# Revit family: Chaine de traitement par Absorption (support au sol) - AD5325
name_source: partatom
category: Equipement spécialisé
revit_build: Autodesk Revit 2018 (Build: 20170223_1515(x64)
units: mm (PartAtom-declared; Revit-internal decimal feet)

## family parameters
Basée sur le plan de construction = Non
Cote de connecteur circulaire = Utiliser le diamètre
Couper avec des vides une fois chargée = Non
Partagée = Non
Point de calcul de pièce = Non
Toujours verticalement = Oui
Type d'élément = Normal

## types (1)
- SEC 7 HC - AD 5325
    COS_PHI = 0.9
    DEBIT_ENTREE_AIR = 325.0 m³/h
    DEBIT_SORTIE_AIR = 325.0 m³/h
    DESCR_ALIM_X = Alimentation X ; ID 3G1mm² ;
    DESCR_ENTREE_AIR = Entrée Air ; 325 m3/h à 10 bar ; ID G 1"1/4 ;
    DESCR_SORTIE_AIR = Sortie Air ; 325 m3/h à 10 bar ; ID G 1"1/4 ;
    DIAM_ENTREE_AIR = 32 mm  [stored 0.104987 ft]
    DIAM_SORTIE_AIR = 32 mm  [stored 0.104987 ft]
    Diametre_Percement_Fixation_Sol = 14 mm  [stored 0.0459318 ft]
    E1 = 140 mm  [stored 0.459318 ft]
    E2 = 35 mm  [stored 0.114829 ft]
    Entraxe_Barres_Horizontales = 560 mm  [stored 1.83727 ft]
    Entraxe_Barres_Verticales = 310 mm  [stored 1.01706 ft]
    Entraxe_Horizontal_Fixation_Sol = 730 mm  [stored 2.39501 ft]
    Entraxe_Manomètres = 100 mm  [stored 0.328084 ft]
    Entraxe_Rouleaux = 390 mm  [stored 1.27953 ft]
    Entraxe_Vertical_Fixation_Sol = 470 mm  [stored 1.54199 ft]
    Epaisseur_Barre_Support = 70 mm  [stored 0.229659 ft]
    Epaisseur_Cache = 20 mm  [stored 0.0656168 ft]
    FREQUENCE = 50 Hz
    Fabricant = MIL'S
    HAUTEUR = 1690 mm  [stored 5.54462 ft]
    Hauteur_Manomètres = 1500 mm  [stored 4.92126 ft]
    Hauteur_Rouleau = 1520 mm  [stored 4.98688 ft]
    Hauteur_Sol_Barres = 135 mm  [stored 0.442913 ft]
    Hauteur_Totale = 1690 mm  [stored 5.54462 ft]
    LARGEUR = 760 mm  [stored 2.49344 ft]
    LONGUEUR = 560 mm  [stored 1.83727 ft]
    Largeur_Panneaux_Support = 460 mm  [stored 1.50919 ft]
    Largeur_Totale = 760 mm  [stored 2.49344 ft]
    Lien espace client = https://www.mils.fr
    Modèle = SEC 7 HC - AD 5325
    NBR_POLES = 1
    NEUTRE = Oui
    POIDS(Kg) = 257 mm  [stored 0.843176 ft]
    PROTEC_ELECT_X = Disjoncteur courbe D - 1 A
    PUISS_APPARENTE_X = 167 VA
    PUISS_ELECT_X = 0 kW
    Profondeur_Totale = 560 mm  [stored 1.83727 ft]
    Rayon_Percement_Fixation_Sol = 7 mm  [stored 0.0229659 ft]
    Rayon_Raccord_Face_Avant = 40 mm  [stored 0.131234 ft]
    TENSION_ALIM = 230 V
    TERRE = Oui

note: [stored X ft] marks values corroborated as IEEE doubles in the binary element streams (Revit-internal decimal feet)
